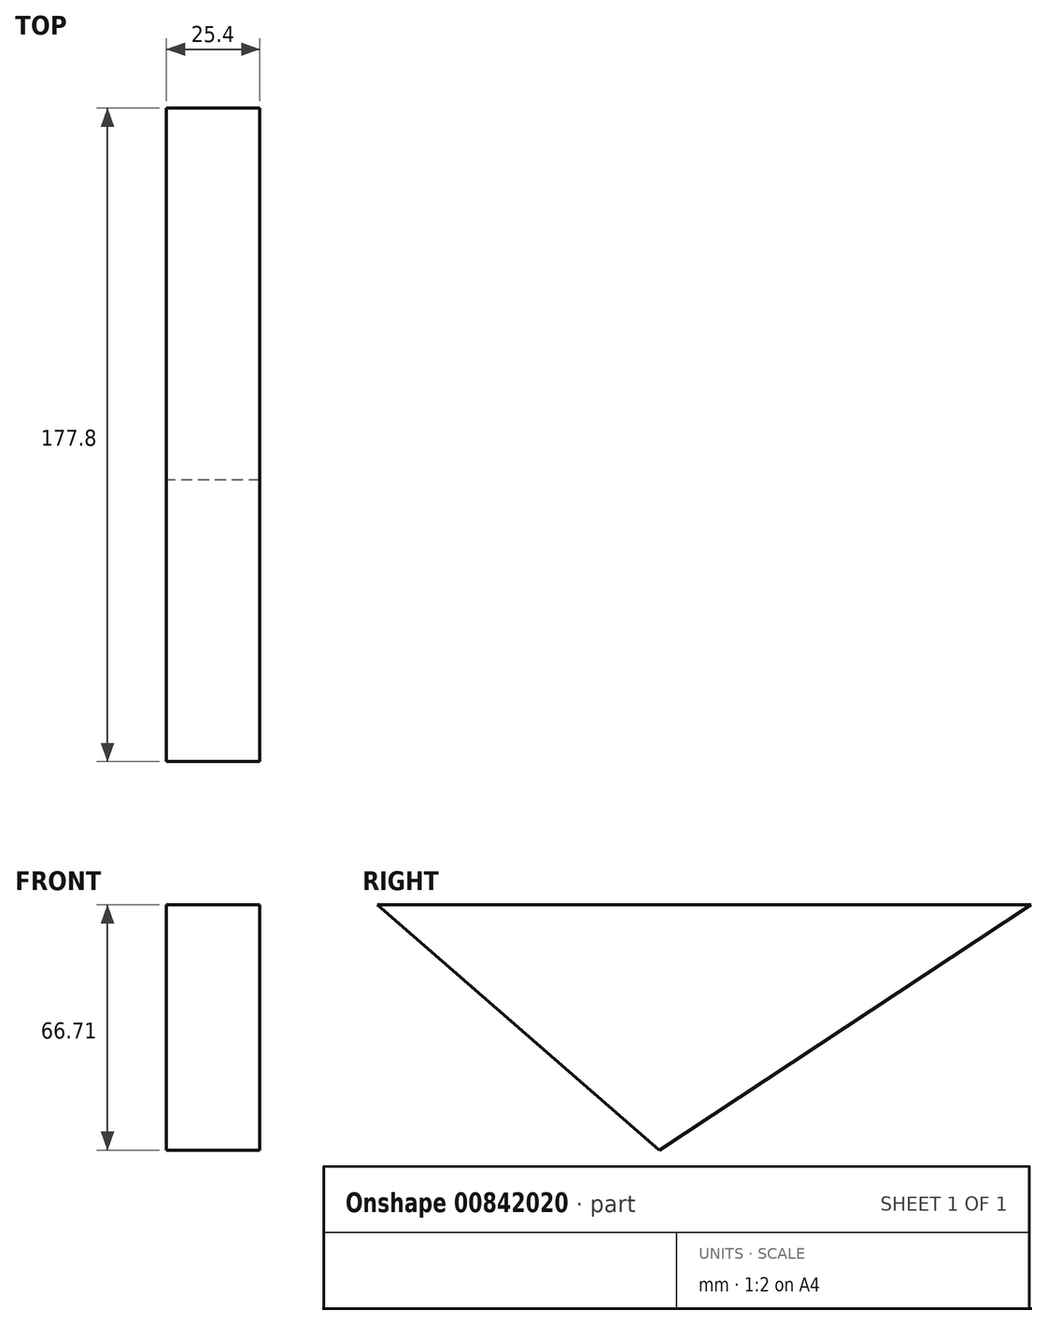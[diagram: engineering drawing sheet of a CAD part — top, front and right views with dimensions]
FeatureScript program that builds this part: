
annotation { "Feature Type Name" : "Feature", "Feature Type Description" : "" }
export const myFeature = defineFeature(function(context is Context, id is Id, definition is map)
    precondition{}
    {
        {
            var Q0;
            Q0=qCreatedBy(makeId("Right.planeOp"),FACE);
            var sketch = newSketch(context, id + "F0", { "sketchPlane" : qUnion([Q0])});
            skLineSegment(sketch, "E0", {"start": v(0, 0) * mm, "end": v(-76.63, 66.7) * mm});
            skLineSegment(sketch, "E1", {"start": v(-76.63, 66.7) * mm, "end": v(101.17, 66.7) * mm});
            skLineSegment(sketch, "E2", {"start": v(101.17, 66.7) * mm, "end": v(0, 0) * mm});
            skSolve(sketch);
        }
        {
            var Q0;
            Q0=makeQuery(id+"F0.imprint","IMPRINT",FACE,{"disambiguationData":[TD([[makeQuery(id+"F0.imprint","IMPRINT",EDGE,{"derivedFrom":sQuery(id+"F0.wireOp",EDGE,"E0")}),-1.0]])]});
            extrude(context, id + "F1", {"entities" : qUnion([Q0]), "depth" : 25.4 * mm, "offsetDistance" : 25.4 * mm});
        }
    });
